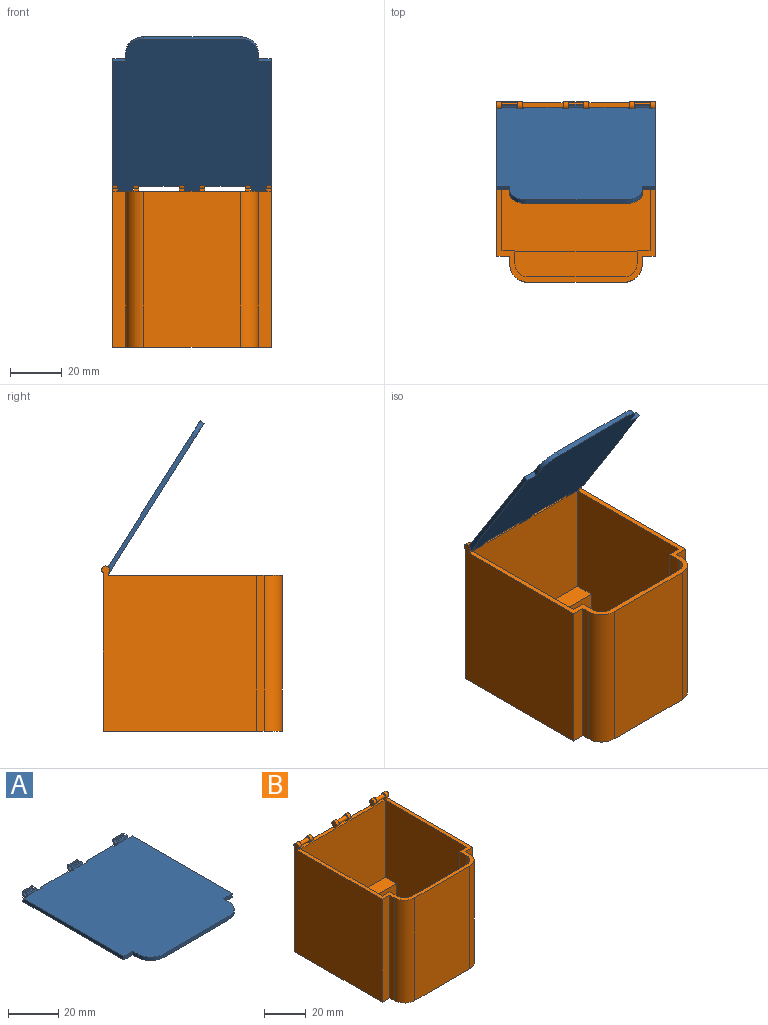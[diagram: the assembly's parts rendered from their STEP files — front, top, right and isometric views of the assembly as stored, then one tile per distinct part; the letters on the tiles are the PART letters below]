
ASSEMBLY  parts=2 mates=1
PART A: 56 faces, bbox 61x69.5x2.8 mm
  f0: cylinder r=1.5mm len=5.5mm, axis (-1,0,0), area 12.1mm2, adj f3,f4,f5,f7
  f1: cylinder r=1.5mm len=5.5mm, axis (-1,0,0), area 5.8mm2, adj f3,f4,f6,f8
  f2: cylinder r=1mm len=5.5mm, axis (-1,0,0), area 29.2mm2, adj f3,f4,f6,f7
  f3: plane 3.25x2.75mm, normal (1,0,0), area 4.4mm2, adj f0,f1,f2,f5,f6,f7,f8,f43
  f4: plane 3x2.75mm, normal (-1,0,0), area 3.7mm2, adj f0,f1,f2,f5,f6,f7,f8,f9
  f5: plane 5.5x0.75mm, normal (0,1,0), area 4.1mm2, adj f0,f3,f4,f55
  f6: plane 5.5x0.74mm, normal (0,0,1), area 4.1mm2, adj f1,f2,f3,f4
  f7: plane 5.5x0.74mm, normal (0,0,1), area 4.1mm2, adj f0,f2,f3,f4
  f8: plane 67x61mm, normal (0,0,1), area 3947.1mm2, adj f1,f3,f4,f9,f11,f13,f14,f19
  f9: cylinder r=1mm len=0.54mm, axis (1,0,0), area 0.2mm2, adj f4,f8,f28,f38
  f10: cylinder r=1.5mm len=5.5mm, axis (-1,0,0), area 12.1mm2, adj f13,f14,f15,f17
  f11: cylinder r=1.5mm len=5.5mm, axis (-1,0,0), area 5.8mm2, adj f8,f13,f14,f16
  f12: cylinder r=1mm len=5.5mm, axis (-1,0,0), area 29.2mm2, adj f13,f14,f16,f17
  f13: plane 3.25x2.75mm, normal (1,0,0), area 4.4mm2, adj f8,f10,f11,f12,f15,f16,f17,f39
  f14: plane 3.25x2.75mm, normal (-1,0,0), area 4.4mm2, adj f8,f10,f11,f12,f15,f16,f17,f41
  f15: plane 5.5x0.75mm, normal (0,1,0), area 4.1mm2, adj f10,f13,f14,f55
  f16: plane 5.5x0.74mm, normal (0,0,1), area 4.1mm2, adj f11,f12,f13,f14
  f17: plane 5.5x0.74mm, normal (0,0,1), area 4.1mm2, adj f10,f12,f13,f14
  f18: cylinder r=1.5mm len=5.5mm, axis (-1,0,0), area 12.1mm2, adj f21,f22,f23,f25
  f19: cylinder r=1.5mm len=5.5mm, axis (-1,0,0), area 5.8mm2, adj f8,f21,f22,f24
  f20: cylinder r=1mm len=5.5mm, axis (-1,0,0), area 29.2mm2, adj f21,f22,f24,f25
  f21: plane 3.25x2.75mm, normal (1,0,0), area 4.4mm2, adj f8,f18,f19,f20,f23,f24,f25,f47
  f22: plane 3.25x2.75mm, normal (-1,0,0), area 4.4mm2, adj f8,f18,f19,f20,f23,f24,f25,f49
  f23: plane 5.5x0.75mm, normal (0,1,0), area 4.1mm2, adj f18,f21,f22,f55
  f24: plane 5.5x0.74mm, normal (0,0,1), area 4.1mm2, adj f19,f20,f21,f22
  f25: plane 5.5x0.74mm, normal (0,0,1), area 4.1mm2, adj f18,f20,f21,f22
  f26: plane 15x1.75mm, normal (0,1,0), area 26.3mm2, adj f8,f51,f54,f55
  f27: plane 15x1.75mm, normal (0,1,0), area 26.3mm2, adj f8,f52,f53,f55
  f28: plane 1.21x0.25mm, normal (0,1,0), area 0.3mm2, adj f4,f9,f38,f55
  f29: plane 56.75x1.75mm, normal (1,0,0), area 99mm2, adj f8,f37,f39,f40,f55
  f30: plane 56.75x1.75mm, normal (-1,0,0), area 99mm2, adj f8,f31,f45,f46,f55
  f31: plane 5x1.75mm, normal (0,-1,0), area 8.8mm2, adj f8,f30,f32,f55
  f32: plane 3x1.75mm, normal (-1,0,0), area 5.2mm2, adj f8,f31,f33,f55
  f33: cylinder r=7mm len=7mm, axis (0,0,-1), area 19.2mm2, adj f8,f32,f34,f55
  f34: plane 37x1.75mm, normal (0,-1,0), area 64.8mm2, adj f8,f33,f35,f55
  f35: cylinder r=7mm len=7mm, axis (0,0,-1), area 19.2mm2, adj f8,f34,f36,f55
  f36: plane 3x1.75mm, normal (1,0,0), area 5.3mm2, adj f8,f35,f37,f55
  f37: plane 5x1.75mm, normal (0,-1,0), area 8.8mm2, adj f8,f29,f36,f55
  f38: plane 1.75x0.75mm, normal (-1,0,0), area 0.7mm2, adj f8,f9,f28,f45,f46,f55
  f39: cylinder r=1.5mm len=2.25mm, axis (-1,0,0), area 2.6mm2, adj f8,f13,f29,f40
  f40: plane 2.25x0.75mm, normal (0,1,0), area 1.7mm2, adj f13,f29,f39,f55
  f41: plane 2.5x0.75mm, normal (0,1,0), area 1.9mm2, adj f14,f42,f51,f55
  f42: cylinder r=1.5mm len=2.5mm, axis (-1,0,0), area 2.9mm2, adj f8,f14,f41,f51
  f43: plane 2.5x0.75mm, normal (0,1,0), area 1.9mm2, adj f3,f44,f52,f55
  f44: cylinder r=1.5mm len=2.5mm, axis (-1,0,0), area 2.9mm2, adj f3,f8,f43,f52
  f45: cylinder r=1.5mm len=2mm, axis (-1,0,0), area 2.3mm2, adj f8,f30,f38,f46
  f46: plane 2x0.75mm, normal (0,1,0), area 1.5mm2, adj f30,f38,f45,f55
  f47: plane 2.5x0.75mm, normal (0,1,0), area 1.9mm2, adj f21,f48,f54,f55
  f48: cylinder r=1.5mm len=2.5mm, axis (-1,0,0), area 2.9mm2, adj f8,f21,f47,f54
  f49: plane 2.5x0.75mm, normal (0,1,0), area 1.9mm2, adj f22,f50,f53,f55
  f50: cylinder r=1.5mm len=2.5mm, axis (-1,0,0), area 2.9mm2, adj f8,f22,f49,f53
  f51: plane 1.75x0.75mm, normal (1,0,0), area 0.8mm2, adj f8,f26,f41,f42,f55
  f52: plane 1.75x0.75mm, normal (-1,0,0), area 0.8mm2, adj f8,f27,f43,f44,f55
  f53: plane 1.75x0.75mm, normal (1,0,0), area 0.8mm2, adj f8,f27,f49,f50,f55
  f54: plane 1.75x0.75mm, normal (-1,0,0), area 0.8mm2, adj f8,f26,f47,f48,f55
  f55: plane 69x61mm, normal (0,0,-1), area 3995.4mm2, adj f3,f4,f5,f13,f14,f15,f21,f22
PART B: 51 faces, bbox 61x69.5x63.6 mm
  f0: plane 15.5x2mm, normal (0,0,1), area 31mm2, adj f6,f17,f35,f45
  f1: plane 6x2mm, normal (0,0,1), area 12mm2, adj f6,f17,f47,f48
  f2: plane 67x61mm, normal (0,0,1), area 371.7mm2, adj f7,f8,f9,f10,f11,f12,f13,f14
  f3: plane 6x2mm, normal (0,0,1), area 12mm2, adj f6,f17,f40,f41
  f4: plane 15.5x2mm, normal (0,0,1), area 31mm2, adj f6,f17,f31,f42
  f5: plane 6x2mm, normal (0,0,1), area 12mm2, adj f6,f17,f33,f34
  f6: plane 61x61mm, normal (0,1,0), area 3672mm2, adj f0,f1,f3,f4,f5,f7,f24,f29
  f7: plane 63.62x59.5mm, normal (-1,0,0), area 3548.5mm2, adj f2,f6,f8,f29,f49,f50
  f8: plane 60x5mm, normal (0,-1,0), area 300mm2, adj f2,f7,f9,f29
  f9: plane 60x3mm, normal (-1,0,0), area 180mm2, adj f2,f8,f10,f29
  f10: cylinder r=7mm len=60mm, axis (0,0,-1), area 659.7mm2, adj f2,f9,f11,f29
  f11: plane 60x37mm, normal (0,-1,0), area 2220mm2, adj f2,f10,f12,f29
  f12: cylinder r=7mm len=60mm, axis (0,0,-1), area 659.7mm2, adj f2,f11,f13,f29
  f13: plane 60x3mm, normal (1,0,0), area 180mm2, adj f2,f12,f14,f29
  f14: plane 60x5mm, normal (0,-1,0), area 300mm2, adj f2,f13,f24,f29
  f15: plane 45x5mm, normal (1,0,0), area 225mm2, adj f2,f19,f23,f27
  f16: plane 58x55mm, normal (1,0,0), area 3092.5mm2, adj f2,f17,f19,f25,f26,f28
  f17: plane 57x46mm, normal (0,-1,0), area 2573mm2, adj f0,f1,f3,f4,f5,f16,f18,f25
  f18: plane 58x55mm, normal (-1,0,0), area 3092.5mm2, adj f2,f17,f19,f25,f26,f28
  f19: plane 58x57mm, normal (0,1,0), area 1191mm2, adj f2,f15,f16,f18,f20,f27,f28
  f20: plane 45x5mm, normal (-1,0,0), area 225mm2, adj f2,f19,f21,f27
  f21: cylinder r=5mm len=45mm, axis (0,0,-1), area 353.4mm2, adj f2,f20,f22,f27
  f22: plane 45x37mm, normal (0,1,0), area 1665mm2, adj f2,f21,f23,f27
  f23: cylinder r=5mm len=45mm, axis (0,0,-1), area 353.4mm2, adj f2,f15,f22,f27
  f24: plane 63.62x59.5mm, normal (1,0,0), area 3548.5mm2, adj f2,f6,f14,f29,f37,f38
  f25: plane 57x7.5mm, normal (0,0,1), area 427.5mm2, adj f16,f17,f18,f26
  f26: plane 57x13mm, normal (0,-1,0), area 741mm2, adj f16,f18,f25,f28
  f27: plane 47x10mm, normal (0,0,1), area 459.3mm2, adj f15,f19,f20,f21,f22,f23
  f28: plane 57x47.5mm, normal (0,0,1), area 2707.5mm2, adj f16,f18,f19,f26
  f29: plane 69x61mm, normal (0,0,-1), area 4088mm2, adj f6,f7,f8,f9,f10,f11,f12,f13
  f30: cylinder r=1.5mm len=3mm, axis (-1,0,0), area 14.5mm2, adj f6,f17,f31,f34
  f31: plane 3.62x3mm, normal (1,0,0), area 8.5mm2, adj f4,f6,f17,f30
  f32: cylinder r=1mm len=6mm, axis (1,0,0), area 37.7mm2, adj f33,f34
  f33: plane 3.62x3mm, normal (1,0,0), area 5.4mm2, adj f5,f6,f17,f32,f36
  f34: plane 3.62x3mm, normal (-1,0,0), area 5.4mm2, adj f5,f6,f17,f30,f32
  f35: plane 3.62x3mm, normal (-1,0,0), area 8.5mm2, adj f0,f6,f17,f36
  f36: cylinder r=1.5mm len=3mm, axis (-1,0,0), area 14.5mm2, adj f6,f17,f33,f35
  f37: cylinder r=1.5mm len=3mm, axis (-1,0,0), area 14.5mm2, adj f6,f24,f38,f41
  f38: plane 2x1mm, normal (0,-1,0), area 2mm2, adj f2,f24,f37,f41
  f39: cylinder r=1mm len=6mm, axis (1,0,0), area 37.7mm2, adj f40,f41
  f40: plane 3.62x3mm, normal (1,0,0), area 5.4mm2, adj f3,f6,f17,f39,f43
  f41: plane 3.62x3mm, normal (-1,0,0), area 5.4mm2, adj f3,f6,f37,f38,f39
  f42: plane 3.62x3mm, normal (-1,0,0), area 8.5mm2, adj f4,f6,f17,f43
  f43: cylinder r=1.5mm len=3mm, axis (-1,0,0), area 14.5mm2, adj f6,f17,f40,f42
  f44: cylinder r=1.5mm len=3mm, axis (-1,0,0), area 14.5mm2, adj f6,f17,f45,f48
  f45: plane 3.62x3mm, normal (1,0,0), area 8.5mm2, adj f0,f6,f17,f44
  f46: cylinder r=1mm len=6mm, axis (1,0,0), area 37.7mm2, adj f47,f48
  f47: plane 3.62x3mm, normal (1,0,0), area 5.4mm2, adj f1,f6,f46,f49,f50
  f48: plane 3.62x3mm, normal (-1,0,0), area 5.4mm2, adj f1,f6,f17,f44,f46
  f49: plane 2x1mm, normal (0,-1,0), area 2mm2, adj f2,f7,f47,f50
  f50: cylinder r=1.5mm len=3mm, axis (-1,0,0), area 14.5mm2, adj f6,f7,f47,f49
PLACE A rot(axis=(-1,0,0),57.7deg) t=(0,-24.23,50.23)mm
PLACE B at identity fixed
MATE revolute B.f30 <-> A.f0  axis (1,0,0) through (30.5,33.5,47.12)mm
